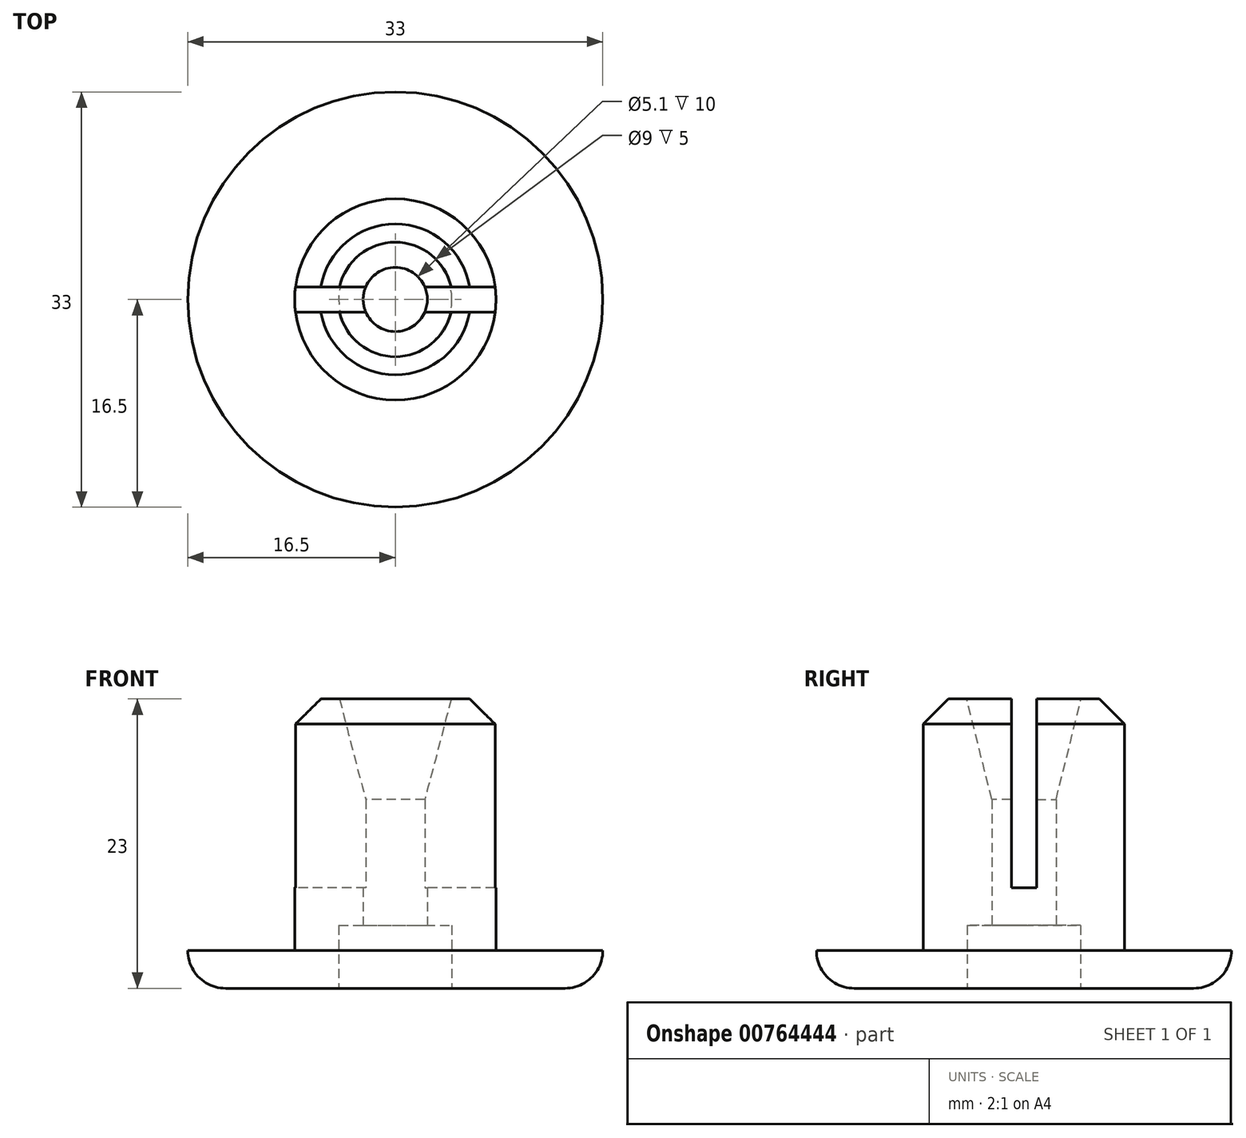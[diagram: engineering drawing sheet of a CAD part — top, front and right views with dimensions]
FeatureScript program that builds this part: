
annotation { "Feature Type Name" : "Feature", "Feature Type Description" : "" }
export const myFeature = defineFeature(function(context is Context, id is Id, definition is map)
    precondition{}
    {
        {
            var Q0;
            Q0=qCreatedBy(makeId("Top.planeOp"),FACE);
            var sketch = newSketch(context, id + "F0", { "sketchPlane" : qUnion([Q0])});
            skCircle(sketch, "E0", {"center": v(0, 0) * mm, "radius": 16.5 * mm});
            skSolve(sketch);
        }
        {
            var Q0;
            Q0 = qSketchRegion(id + "F0", true);
            extrude(context, id + "F1", {"entities" : qUnion([Q0]), "depth" : 3 * mm, "offsetDistance" : 25 * mm});
        }
        {
            var Q0;
            Q0=makeQuery(id+"F1.opExtrude","CAP_FACE",FACE,{"disambiguationData":[OSD([sQuery(id+"F0.wireOp",EDGE,"E0")])],"isStart":false});
            var sketch = newSketch(context, id + "F2", { "sketchPlane" : qUnion([Q0])});
            skCircle(sketch, "E1", {"center": v(0, 0) * mm, "radius": 8 * mm});
            skSolve(sketch);
        }
        {
            var Q0;
            Q0 = qSketchRegion(id + "F2", true);
            extrude(context, id + "F3", {"entities" : qUnion([Q0]), "operationType" : NewBodyOperationType.ADD, "depth" : 20 * mm, "offsetDistance" : 25 * mm});
        }
        {
            var Q0;
            Q0=makeQuery(id+"F1.opExtrude","CAP_FACE",FACE,{"disambiguationData":[OSD([sQuery(id+"F0.wireOp",EDGE,"E0")])],"isStart":true});
            var sketch = newSketch(context, id + "F4", { "sketchPlane" : qUnion([Q0])});
            skCircle(sketch, "E2", {"center": v(0, 0) * mm, "radius": 2.55 * mm});
            skSolve(sketch);
        }
        {
            var Q0;
            Q0 = qSketchRegion(id + "F4", true);
            extrude(context, id + "F5", {"entities" : qUnion([Q0]), "operationType" : NewBodyOperationType.REMOVE, "oppositeDirection" : true, "depth" : 25 * mm, "offsetDistance" : 25 * mm});
        }
        {
            var Q0;
            Q0=makeQuery(id+"F1.opExtrude","CAP_FACE",FACE,{"disambiguationData":[OSD([sQuery(id+"F0.wireOp",EDGE,"E0")])],"isStart":true});
            var sketch = newSketch(context, id + "F6", { "sketchPlane" : qUnion([Q0])});
            skCircle(sketch, "E3", {"center": v(0, 0) * mm, "radius": 4.5 * mm});
            skSolve(sketch);
        }
        {
            var Q0;
            Q0 = qSketchRegion(id + "F6", true);
            extrude(context, id + "F7", {"entities" : qUnion([Q0]), "operationType" : NewBodyOperationType.REMOVE, "oppositeDirection" : true, "depth" : 5 * mm, "offsetDistance" : 25 * mm});
        }
        {
            var Q0;
            Q0=makeQuery(id+"F3.opExtrude","CAP_FACE",FACE,{"disambiguationData":[OSD([sQuery(id+"F2.wireOp",EDGE,"E1")])],"isStart":false});
            var sketch = newSketch(context, id + "F8", { "sketchPlane" : qUnion([Q0])});
            skLineSegment(sketch, "E4.bottom", {"start": v(8.89, -1) * mm, "end": v(-8.89, -1) * mm});
            skLineSegment(sketch, "E4.top", {"start": v(8.89, 1) * mm, "end": v(-8.89, 1) * mm});
            skLineSegment(sketch, "E4.left", {"start": v(8.89, -1) * mm, "end": v(8.89, 1) * mm});
            skLineSegment(sketch, "E4.right", {"start": v(-8.89, -1) * mm, "end": v(-8.89, 1) * mm});
            skPoint(sketch, "E4.middle", {"position": v(0, 0) * mm});
            skSolve(sketch);
        }
        {
            var Q0;
            Q0 = qSketchRegion(id + "F8", true);
            extrude(context, id + "F9", {"entities" : qUnion([Q0]), "operationType" : NewBodyOperationType.REMOVE, "oppositeDirection" : true, "depth" : 15 * mm, "offsetDistance" : 25 * mm});
        }
        {
            var Q0;
            Q0=makeQuery(id+"F1.opExtrude","CAP_EDGE",EDGE,{"disambiguationData":[OSD([sQuery(id+"F0.wireOp",EDGE,"E0")])],"isStart":true});
            fillet(context, id + "F10", {"entities" : qUnion([Q0]), "radius" : 3 * mm, "tangentPropagation" : true, "allowEdgeOverflow" : false});
        }
        {
            var Q0;
            {var subQ0=sQuery(id+"F2.wireOp",EDGE,"E1");Q0=makeQuery(id+"F9.boolean.opBoolean","SPLIT",EDGE,{"disambiguationData":[TD([makeQuery(id+"F9.opExtrude","SWEPT_FACE",FACE,{"disambiguationData":[OSD([sQuery(id+"F8.wireOp",EDGE,"E4.top")])]})])],"derivedFrom":makeQuery(id+"F3.opExtrude","CAP_EDGE",EDGE,{"disambiguationData":[OSD([subQ0])],"isStart":false})});}
            var Q1;
            {var subQ0=sQuery(id+"F2.wireOp",EDGE,"E1");Q1=makeQuery(id+"F9.boolean.opBoolean","SPLIT",EDGE,{"disambiguationData":[TD([makeQuery(id+"F9.opExtrude","SWEPT_FACE",FACE,{"disambiguationData":[OSD([sQuery(id+"F8.wireOp",EDGE,"E4.bottom")])]})])],"derivedFrom":makeQuery(id+"F3.opExtrude","CAP_EDGE",EDGE,{"disambiguationData":[OSD([subQ0])],"isStart":false})});}
            chamfer(context, id + "F11", {"entities" : qUnion([Q0, Q1]), "width" : 2 * mm, "tangentPropagation" : true});
        }
        {
            var Q0;
            {var subQ0=makeQuery(id+"F3.opExtrude","CAP_FACE",FACE,{"disambiguationData":[OSD([sQuery(id+"F2.wireOp",EDGE,"E1")])],"isStart":false});var subQ1=makeQuery(id+"F5.opExtrude","SWEPT_FACE",FACE,{"disambiguationData":[OSD([sQuery(id+"F4.wireOp",EDGE,"E2")])]});Q0=makeQuery(id+"F9.boolean.opBoolean","SPLIT",EDGE,{"disambiguationData":[TD([makeQuery(id+"F9.opExtrude","SWEPT_FACE",FACE,{"disambiguationData":[OSD([sQuery(id+"F8.wireOp",EDGE,"E4.top")])]})])],"derivedFrom":makeQuery(id+"F5.boolean.opBoolean","INTERSECT",EDGE,{"derivedFrom":[subQ0,subQ1]})});}
            var Q1;
            {var subQ0=makeQuery(id+"F3.opExtrude","CAP_FACE",FACE,{"disambiguationData":[OSD([sQuery(id+"F2.wireOp",EDGE,"E1")])],"isStart":false});var subQ1=makeQuery(id+"F5.opExtrude","SWEPT_FACE",FACE,{"disambiguationData":[OSD([sQuery(id+"F4.wireOp",EDGE,"E2")])]});Q1=makeQuery(id+"F9.boolean.opBoolean","SPLIT",EDGE,{"disambiguationData":[TD([makeQuery(id+"F9.opExtrude","SWEPT_FACE",FACE,{"disambiguationData":[OSD([sQuery(id+"F8.wireOp",EDGE,"E4.bottom")])]})])],"derivedFrom":makeQuery(id+"F5.boolean.opBoolean","INTERSECT",EDGE,{"derivedFrom":[subQ0,subQ1]})});}
            chamfer(context, id + "F12", {"entities" : qUnion([Q0, Q1]), "chamferType" : ChamferType.TWO_OFFSETS, "width1" : 8 * mm, "oppositeDirection" : false, "width2" : 2 * mm, "tangentPropagation" : true});
        }
    });
